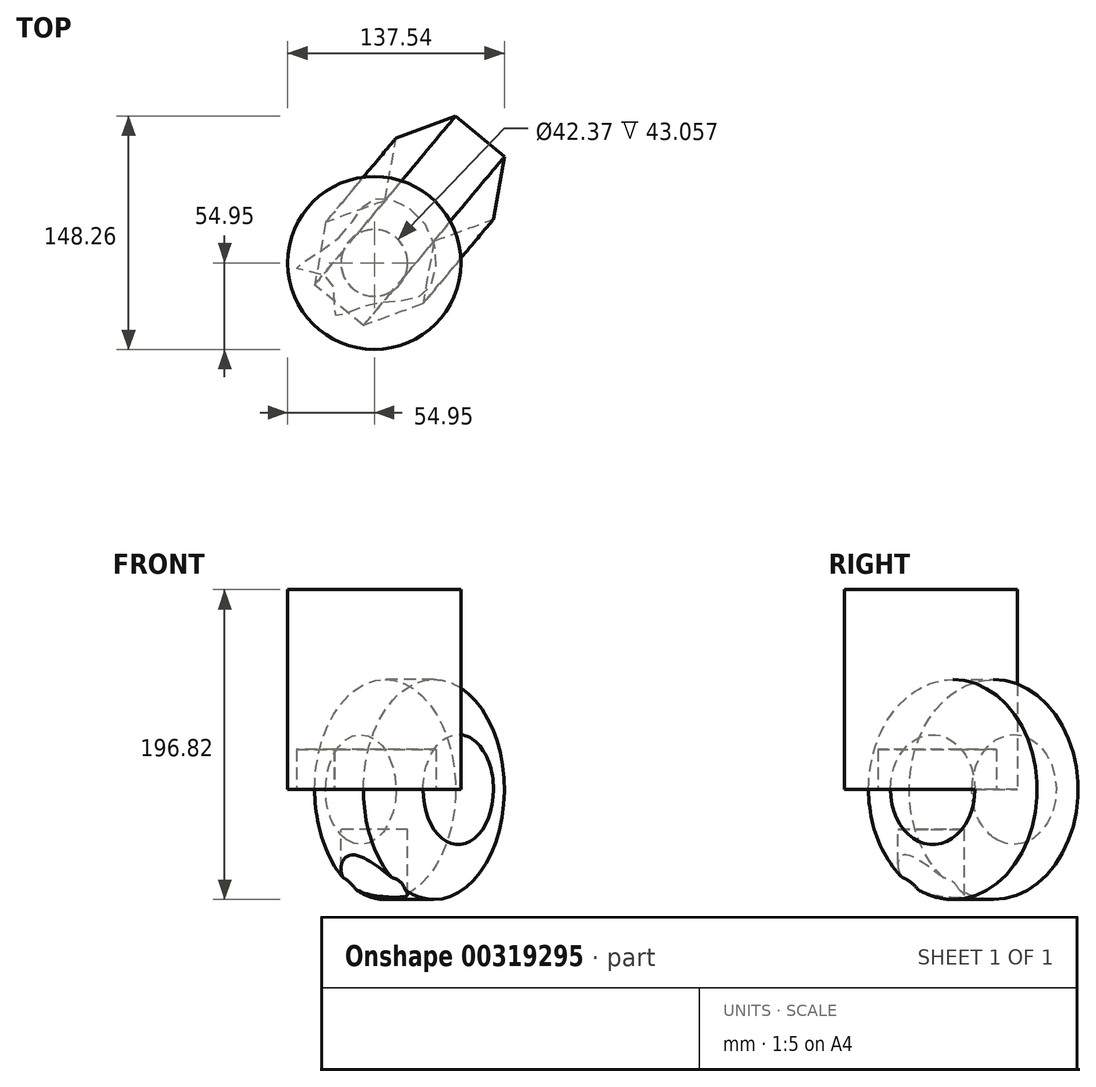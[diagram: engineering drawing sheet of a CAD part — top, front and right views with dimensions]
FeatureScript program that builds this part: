
annotation { "Feature Type Name" : "Feature", "Feature Type Description" : "" }
export const myFeature = defineFeature(function(context is Context, id is Id, definition is map)
    precondition{}
    {
        {
            var Q0;
            Q0=qCreatedBy(makeId("Top.planeOp"),FACE);
            var sketch = newSketch(context, id + "F0", { "sketchPlane" : qUnion([Q0])});
            skCircle(sketch, "E0", {"center": v(0, 0) * mm, "radius": 54.95 * mm});
            skSolve(sketch);
        }
        {
            var Q0;
            Q0 = qSketchRegion(id + "F0", true);
            extrude(context, id + "F1", {"entities" : qUnion([Q0]), "depth" : 127 * mm});
        }
        {
            var Q0;
            Q0=qCreatedBy(makeId("Top.planeOp"),FACE);
            var sketch = newSketch(context, id + "F2", { "sketchPlane" : qUnion([Q0])});
            skCircle(sketch, "E1.cCircle", {"center": v(0, 0) * mm, "radius": 34.9 * mm, "construction": true});
            skLineSegment(sketch, "E1.0", {"start": v(37.84, 13.88) * mm, "end": v(30.94, -25.83) * mm});
            skLineSegment(sketch, "E1.1", {"start": v(30.94, -25.83) * mm, "end": v(-6.9, -39.71) * mm});
            skLineSegment(sketch, "E1.2", {"start": v(-6.9, -39.71) * mm, "end": v(-37.84, -13.88) * mm});
            skLineSegment(sketch, "E1.3", {"start": v(-37.84, -13.88) * mm, "end": v(-30.94, 25.83) * mm});
            skLineSegment(sketch, "E1.4", {"start": v(-30.94, 25.83) * mm, "end": v(6.9, 39.71) * mm});
            skLineSegment(sketch, "E1.5", {"start": v(6.9, 39.71) * mm, "end": v(37.84, 13.88) * mm});
            skPoint(sketch, "E1.0.midPoint", {"position": v(34.4, -5.98) * mm});
            skSolve(sketch);
        }
        {
            var Q0;
            Q0 = qSketchRegion(id + "F2", true);
            var Q1;
            Q1=sQuery(id+"F2.wireOp",EDGE,"E1.5");
            revolve(context, id + "F3", {"entities" : qUnion([Q0]), "axis" : qUnion([Q1]), "revolveType" : RevolveType.FULL});
        }
        {
            var Q0;
            Q0=qCreatedBy(makeId("Top.planeOp"),FACE);
            var sketch = newSketch(context, id + "F4", { "sketchPlane" : qUnion([Q0])});
            skCircle(sketch, "E2", {"center": v(0, 0) * mm, "radius": 21.18 * mm});
            skSolve(sketch);
        }
        {
            var Q0;
            Q0 = qSketchRegion(id + "F4", true);
            extrude(context, id + "F5", {"entities" : qUnion([Q0]), "operationType" : NewBodyOperationType.REMOVE, "oppositeDirection" : true, "depth" : 101.6 * mm, "hasSecondDirection" : true, "secondDirectionOppositeDirection" : true, "secondDirectionDepth" : 25.4 * mm});
        }
        {
            var Q0;
            Q0=qCreatedBy(makeId("Top.planeOp"),FACE);
            var sketch = newSketch(context, id + "F6", { "sketchPlane" : qUnion([Q0])});
            skFitSpline(sketch, "E3", {"points": [v(-22.42, 16.17) * mm, v(0, 40.81) * mm, v(33.67, 22.33) * mm, v(32.05, -19.16) * mm, v(-4.26, -26.62) * mm, v(-24.69, -33.1) * mm, v(-27.93, -10.4) * mm, v(-49.33, -3.6) * mm, v(-22.42, 16.17) * mm]});
            skSolve(sketch);
        }
        {
            var Q0;
            Q0 = qSketchRegion(id + "F6", true);
            extrude(context, id + "F7", {"entities" : qUnion([Q0]), "depth" : 25.4 * mm});
        }
        {
            var Q0;
            Q0=sQuery(id+"F6.wireOp",EDGE,"E3");
            extrude(context, id + "F8", {"bodyType" : ToolBodyType.SURFACE, "surfaceEntities" : qUnion([Q0]), "depth" : 25.4 * mm});
        }
    });
